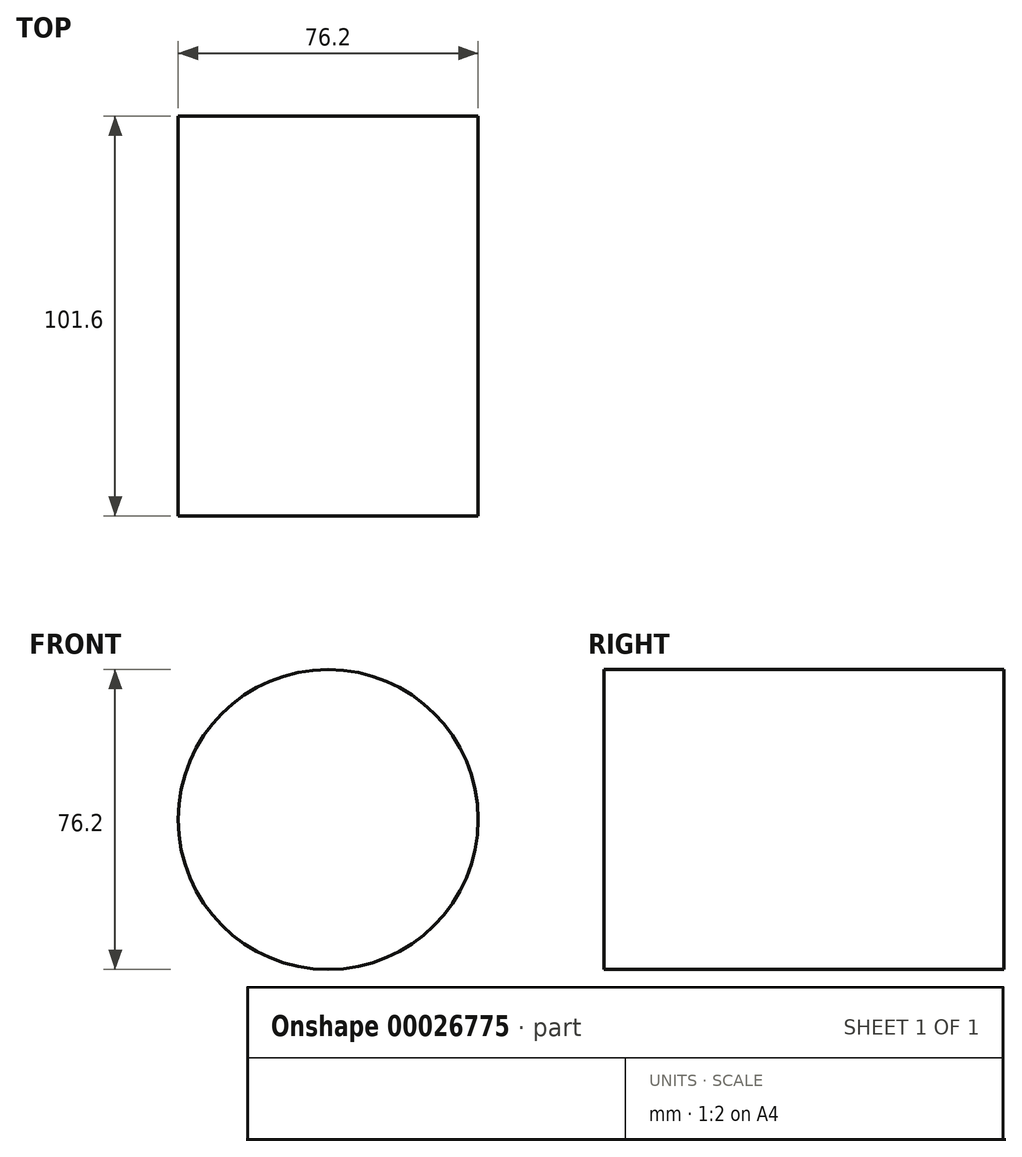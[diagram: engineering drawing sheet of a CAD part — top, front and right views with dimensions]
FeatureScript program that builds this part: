
annotation { "Feature Type Name" : "Feature", "Feature Type Description" : "" }
export const myFeature = defineFeature(function(context is Context, id is Id, definition is map)
    precondition{}
    {
        {
            var Q0;
            Q0=qCreatedBy(makeId("Front.planeOp"),FACE);
            var sketch = newSketch(context, id + "F0", { "sketchPlane" : qUnion([Q0])});
            skCircle(sketch, "E0", {"center": v(0, 0) * mm, "radius": 38.1 * mm});
            skSolve(sketch);
        }
        {
            var Q0;
            Q0 = qSketchRegion(id + "F0", true);
            extrude(context, id + "F1", {"entities" : qUnion([Q0]), "depth" : 101.6 * mm});
        }
    });
